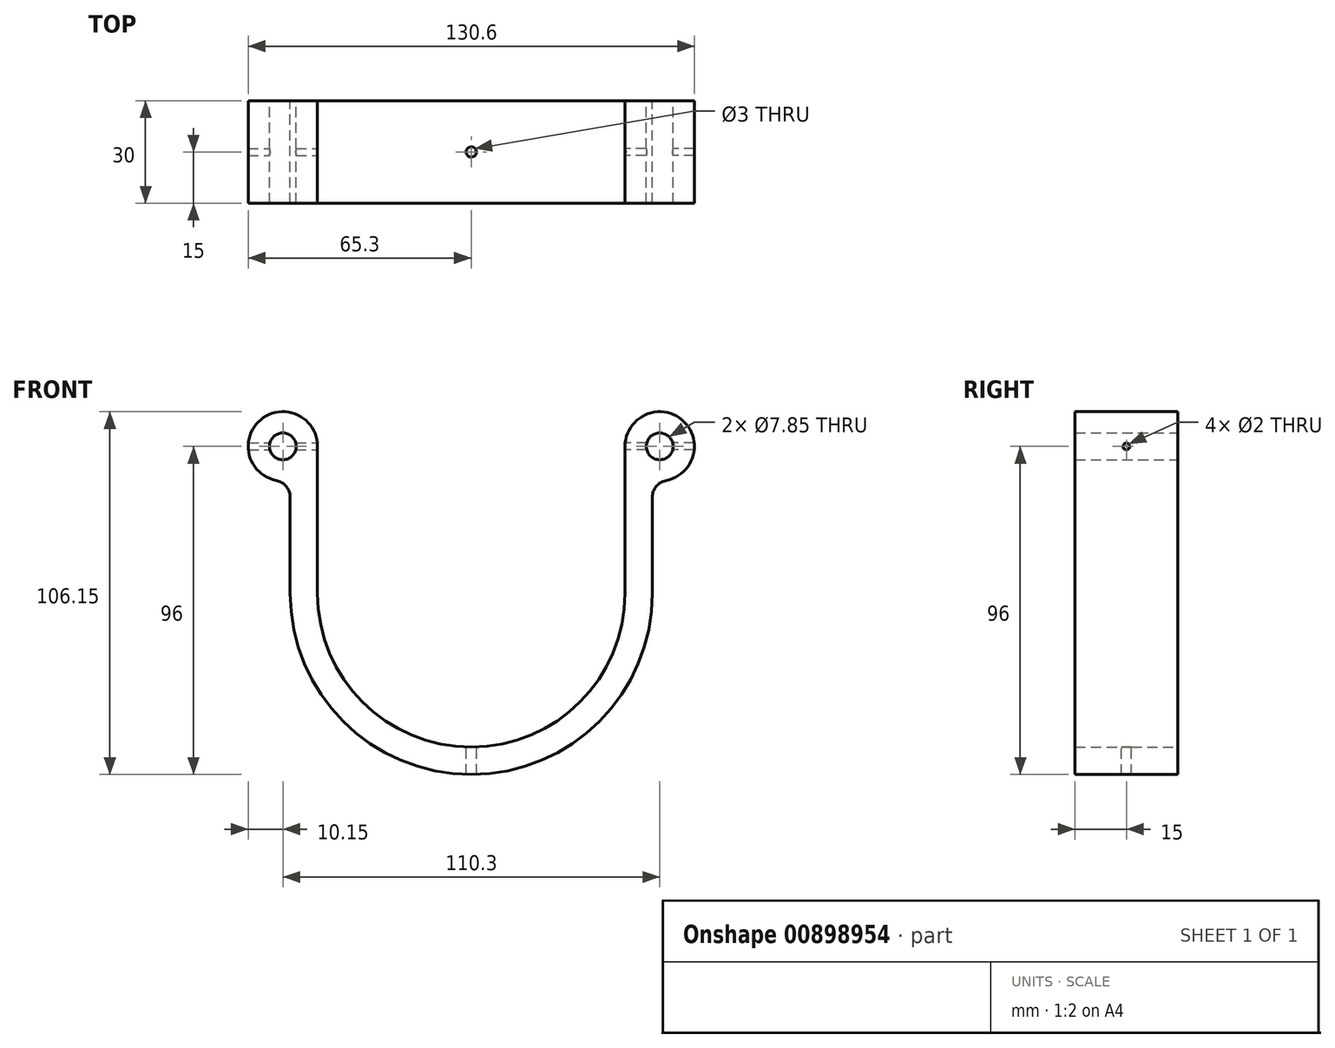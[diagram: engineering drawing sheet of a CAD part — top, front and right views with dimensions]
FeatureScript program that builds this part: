
annotation { "Feature Type Name" : "Feature", "Feature Type Description" : "" }
export const myFeature = defineFeature(function(context is Context, id is Id, definition is map)
    precondition{}
    {
        {
            var Q0;
            Q0=qCreatedBy(makeId("Front.planeOp"),FACE);
            var sketch = newSketch(context, id + "F0", { "sketchPlane" : qUnion([Q0])});
            skLineSegment(sketch, "E0", {"start": v(-45, 0) * mm, "end": v(-45, -43) * mm});
            skLineSegment(sketch, "E1.MirrorCS", {"start": v(45, 0) * mm, "end": v(45, -43) * mm});
            skArc(sketch, "E2", {"start": v(-45, -43) * mm, "mid": v(0, -88) * mm, "end": v(45, -43) * mm});
            skCircle(sketch, "E3", {"center": v(-55.15, 0) * mm, "radius": 3.92 * mm});
            skArc(sketch, "E4.0", {"start": v(-53, -43) * mm, "mid": v(0, -96) * mm, "end": v(53, -43) * mm});
            skArc(sketch, "E5", {"start": v(-45, 0) * mm, "mid": v(-61.62, 7.82) * mm, "end": v(-57.06, -9.97) * mm});
            skLineSegment(sketch, "E6", {"start": v(-53, -43) * mm, "end": v(-53, -14.88) * mm});
            skPoint(sketch, "E7.visualSharp", {"position": v(-53, -9.92) * mm});
            skArc(sketch, "E7.filletArc", {"start": v(-53, -14.88) * mm, "mid": v(-54.15, -11.7) * mm, "end": v(-57.06, -9.97) * mm});
            skCircle(sketch, "E8.MirrorC", {"center": v(55.15, 0) * mm, "radius": 3.92 * mm});
            skArc(sketch, "E9.MirrorCS", {"start": v(45, 0) * mm, "mid": v(61.62, 7.82) * mm, "end": v(57.06, -9.97) * mm});
            skArc(sketch, "E10.MirrorCS", {"start": v(53, -14.88) * mm, "mid": v(54.15, -11.7) * mm, "end": v(57.06, -9.97) * mm});
            skLineSegment(sketch, "E11.MirrorCS", {"start": v(53, -43) * mm, "end": v(53, -14.88) * mm});
            skSolve(sketch);
        }
        {
            var Q0;
            Q0=makeQuery(id+"F0.imprint","IMPRINT",FACE,{"disambiguationData":[TD([[makeQuery(id+"F0.imprint","IMPRINT",EDGE,{"derivedFrom":sQuery(id+"F0.wireOp",EDGE,"E0")}),-1.0]])]});
            extrude(context, id + "F1", {"entities" : qUnion([Q0]), "depth" : 30 * mm, "offsetDistance" : 25 * mm});
        }
        {
            var Q0;
            Q0=qCreatedBy(makeId("Top.planeOp"),FACE);
            var sketch = newSketch(context, id + "F2", { "sketchPlane" : qUnion([Q0])});
            skCircle(sketch, "E12", {"center": v(0, -15) * mm, "radius": 1.5 * mm});
            skSolve(sketch);
        }
        {
            var Q0;
            Q0=qSketchRegion(id+"F2",true);
            extrude(context, id + "F3", {"entities" : qUnion([Q0]), "operationType" : NewBodyOperationType.REMOVE, "endBound" : BoundingType.THROUGH_ALL, "oppositeDirection" : true, "depth" : 25 * mm, "offsetDistance" : 25 * mm});
        }
        {
            var Q0;
            Q0=qCreatedBy(makeId("Right.planeOp"),FACE);
            var sketch = newSketch(context, id + "F4", { "sketchPlane" : qUnion([Q0])});
            skCircle(sketch, "E13", {"center": v(-15, 0) * mm, "radius": 1 * mm});
            skSolve(sketch);
        }
        {
            var Q0;
            Q0=qSketchRegion(id+"F4",true);
            extrude(context, id + "F5", {"entities" : qUnion([Q0]), "operationType" : NewBodyOperationType.REMOVE, "endBound" : BoundingType.THROUGH_ALL, "depth" : 60 * mm, "offsetDistance" : 25 * mm});
        }
        {
            var Q0;
            Q0=qSketchRegion(id+"F4",true);
            extrude(context, id + "F6", {"entities" : qUnion([Q0]), "operationType" : NewBodyOperationType.REMOVE, "endBound" : BoundingType.THROUGH_ALL, "oppositeDirection" : true, "depth" : 25 * mm, "offsetDistance" : 25 * mm});
        }
    });
